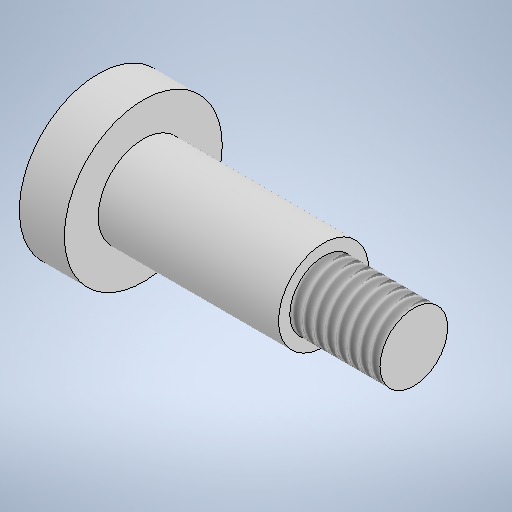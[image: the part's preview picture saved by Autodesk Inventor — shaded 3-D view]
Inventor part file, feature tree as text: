
AUTODESK INVENTOR PART (.ipt)
format: ipt  version: 2025 (Build 290162010, 162A)  size: 267,264 bytes
history: native  units: mm
features: revolve x1, thread x1, sketch x1
ambient origin geometry x8: Origin, YZ Plane, XZ Plane, XY Plane, X Axis, Y Axis, Z Axis, Center Point
bodies: Solid1 (feature_tree)
feature tree (3):
  revolve  "Revolution1"  [1 undecoded]
  thread  "Thread1"  [1 undecoded]
  sketch  "Sketch1"  dims[d0=2.0mm d1=8.0mm d2=4.0mm d3=3.0mm d4=4.0mm d5=7.0mm d6=90.0deg d7=4.0mm d8=0.0mm]
note: 2 required parameter values undecoded (feature->parameter linkage not recoverable at this tier; creation-order binding heuristic only, values carry confidence <= 0.55)